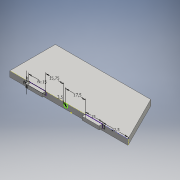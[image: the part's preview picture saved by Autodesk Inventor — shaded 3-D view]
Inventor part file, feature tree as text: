
AUTODESK INVENTOR PART (.ipt)
format: ipt  version: 2016 (Build 200138000, 138)  size: 120,320 bytes
history: native  units: mm
features: extrude x3, sketch x2
ambient origin geometry x8: Origin, YZ Plane, XZ Plane, XY Plane, X Axis, Y Axis, Z Axis, Center Point
bodies: Body1 (feature_tree)
feature tree (5):
  extrude  "Extrusion3"  Depth=40.0mm
  sketch  "Sketch3"  dims[d27=104.0mm d29=84.0mm d30=5.0mm d31=0.0mm d32=22.5mm d33=15.0mm d34=3.0mm d41=15.0mm d42=3.0mm d44=3.5mm d45=15.75mm d46=17.5mm d47=3.0mm d48=0.0mm d49=15.0mm d50=0.0mm d14=1.0mm d15=1.0mm]
  extrude  "Extrusion4"  Depth=15.0mm
  extrude  "Extrusion5"  Depth=5.0mm TaperAngle=0.0deg
  sketch  "Sketch1"  dims[d4=20.0mm d5=40.0mm]
